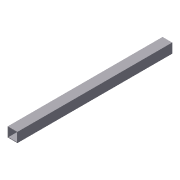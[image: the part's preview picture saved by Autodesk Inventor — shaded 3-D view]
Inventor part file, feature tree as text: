
AUTODESK INVENTOR PART (.ipt)
format: ipt  version: 2012 (Build 160160000, 160)  size: 76,800 bytes
history: native  units: in
note: dims shown in document units (in); Inventor stores cm internally (conversion verified against a paired STEP export)
features: extrude x1, shell x1, sketch x1
ambient origin geometry x8: Origin, YZ Plane, XZ Plane, XY Plane, X Axis, Y Axis, Z Axis, Center Point
bodies: Solid1 (feature_tree)
feature tree (3):
  extrude  "Extrusion1"  Depth=1.0in
  shell  "Shell1"  Thickness=16.0in
  sketch  "Sketch1"  dims[d0=1.0in d1=1.0in d2=16.0in d3=0.0in d4=0.0625in]
